# Revit family: JOMA_Spikplåtsvinklar
name_source: partatom
category: Structural Connections
revit_build: Autodesk Revit Structure 2012 (Build: 20110309_2315(x64)
units: mm (PartAtom-declared; Revit-internal decimal feet)

## types (22) — shared parameters
Länk Joma Dimensioneringsverktyg = http://www.joma.se
Material = Varmförzinkad stålplåt
zero-valued in all types: Default Elevation

## per-type parameters (varying)
| type | Spikplåtsvinkel 5511060 | Spikplåtsvinkel 5511080 | Spikplåtsvinkel 5511100 | Spikplåtsvinkel 5512100 | Spikplåtsvinkel 5546060 & 5524660 | Spikplåtsvinkel 5566060 & 5526660 | Spikplåtsvinkel 5566080 & 5526680 | Spikplåtsvinkel 5566100 & 55266100 | Spikplåtsvinkel 5568060 & 5526860 | Spikplåtsvinkel 5588040 & 5528840 | Spikplåtsvinkel 5588060 & 5528860 | Spikplåtsvinkel 5588080 & 5528880 | Spikplåtsvinkel 5588100 | Spikplåtsvinkel 5588120 | Typ | Vikt | b | h | ir | l | t | yr |
| 5526660  2,0x60x60x60 | No | No | No | No | No | Yes | No | No | No | No | No | No | No | No | SPIKPLÅTSVINKEL 5526660 | 0,11 | 60 mm  [stored 0.19685 ft] | 62 mm | 2.562 mm | 62 mm | 2 mm  [stored 0.00656168 ft] | 4.562 mm |
| 5526680  2,0x60x60x80 | No | No | No | No | No | No | Yes | No | No | No | No | No | No | No | SPIKPLÅTSVINKEL 5526680 | 0,15 | 80 mm | 62 mm | 2.562 mm | 62 mm | 2 mm  [stored 0.00656168 ft] | 4.562 mm |
| 55266100  2,0x60x60x100 | No | No | No | No | No | No | No | Yes | No | No | No | No | No | No | SPIKPLÅTSVINKEL 55266100 | 0,18 | 100 mm  [stored 0.328084 ft] | 62 mm | 2.562 mm | 62 mm | 2 mm  [stored 0.00656168 ft] | 4.562 mm |
| 5528840  2,0x80x80x40 | No | No | No | No | No | No | No | No | No | Yes | No | No | No | No | SPIKPLÅTSVINKEL 5528840 | 0,10 | 40 mm | 82 mm | 2.562 mm | 82 mm | 2 mm  [stored 0.00656168 ft] | 4.562 mm |
| 5528860  2,0x80x80x60 | No | No | No | No | No | No | No | No | No | No | Yes | No | No | No | SPIKPLÅTSVINKEL 5528860 | 0,15 | 60 mm  [stored 0.19685 ft] | 82 mm | 2.562 mm | 82 mm | 2 mm  [stored 0.00656168 ft] | 4.562 mm |
| 5528880  2,0x80x80x80 | No | No | No | No | No | No | No | No | No | No | No | Yes | No | No | SPIKPLÅTSVINKEL 5528880 | 0,19 | 80 mm | 82 mm | 2.562 mm | 82 mm | 2 mm  [stored 0.00656168 ft] | 4.562 mm |
| 5546060  2,5x40x60x60 | No | No | No | No | Yes | No | No | No | No | No | No | No | No | No | SPIKPLÅTSVINKEL 5546060 | 0,11 | 60 mm  [stored 0.19685 ft] | 62.5 mm | 3.203 mm | 42.5 mm | 2.5 mm  [stored 0.0082021 ft] | 5.703 mm |
| 5566060  2,5x60x60x60 | No | No | No | No | No | Yes | No | No | No | No | No | No | No | No | SPIKPLÅTSVINKEL 5566060 | 0,13 | 60 mm  [stored 0.19685 ft] | 62.5 mm | 3.202 mm | 62.5 mm | 2.5 mm  [stored 0.0082021 ft] | 5.702 mm |
| 5566080  2,5x60x60x80 | No | No | No | No | No | No | Yes | No | No | No | No | No | No | No | SPIKPLÅTSVINKEL 5566080 | 0,18 | 80 mm | 62.5 mm | 3.202 mm | 62.5 mm | 2.5 mm  [stored 0.0082021 ft] | 5.702 mm |
| 5566100  2,5x60x60x100 | No | No | No | No | No | No | No | Yes | No | No | No | No | No | No | SPIKPLÅTSVINKEL 5566100 | 0,22 | 100 mm  [stored 0.328084 ft] | 62.5 mm | 3.202 mm | 62.5 mm | 2.5 mm  [stored 0.0082021 ft] | 5.702 mm |
| 5568060  2,5x60x80x60 | No | No | No | No | No | No | No | No | Yes | No | No | No | No | No | SPIKPLÅTSVINKEL 5568060 | 0,15 | 60 mm  [stored 0.19685 ft] | 82.5 mm | 3.203 mm | 62.5 mm | 2.5 mm  [stored 0.0082021 ft] | 5.703 mm |
| 5588040  2,5x80x80x40 | No | No | No | No | No | No | No | No | No | Yes | No | No | No | No | SPIKPLÅTSVINKEL 5588040 | 0,12 | 40 mm | 82.5 mm | 3.202 mm | 82.5 mm | 2.5 mm  [stored 0.0082021 ft] | 5.702 mm |
| 5588060  2,5x80x80x60 | No | No | No | No | No | No | No | No | No | No | Yes | No | No | No | SPIKPLÅTSVINKEL 5588060 | 0,17 | 60 mm  [stored 0.19685 ft] | 82.5 mm | 3.203 mm | 82.5 mm | 2.5 mm  [stored 0.0082021 ft] | 5.703 mm |
| 5588080  2,5x80x80x80 | No | No | No | No | No | No | No | No | No | No | No | Yes | No | No | SPIKPLÅTSVINKEL 5588080 | 0,23 | 80 mm | 82.5 mm | 3.203 mm | 82.5 mm | 2.5 mm  [stored 0.0082021 ft] | 5.703 mm |
| 5588100  2,5x80x80x100 | No | No | No | No | No | No | No | No | No | No | No | No | Yes | No | SPIKPLÅTSVINKEL 5588100 | 0,31 | 100 mm  [stored 0.328084 ft] | 82.5 mm | 3.203 mm | 82.5 mm | 2.5 mm  [stored 0.0082021 ft] | 5.703 mm |
| 5588120  2,5x80x80x120 | No | No | No | No | No | No | No | No | No | No | No | No | No | Yes | SPIKPLÅTSVINKEL 5588120 | 0,34 | 120 mm | 82.5 mm | 3.202 mm | 82.5 mm | 2.5 mm  [stored 0.0082021 ft] | 5.702 mm |
| 5511060  2,5x100x100x60 | Yes | No | No | No | No | No | No | No | No | No | No | No | No | No | SPIKPLÅTSVINKEL 5511060 | 0,21 | 60 mm  [stored 0.19685 ft] | 102.5 mm | 3.203 mm | 102.5 mm | 2.5 mm  [stored 0.0082021 ft] | 5.703 mm |
| 5511080  2,5x100x100x80 | No | Yes | No | No | No | No | No | No | No | No | No | No | No | No | SPIKPLÅTSVINKEL 5511080 | 0,29 | 80 mm | 102.5 mm | 3.203 mm | 102.5 mm | 2.5 mm  [stored 0.0082021 ft] | 5.703 mm |
| 5511100  2,5x100x100x100 | No | No | Yes | No | No | No | No | No | No | No | No | No | No | No | SPIKPLÅTSVINKEL 5511100 | 0,36 | 100 mm  [stored 0.328084 ft] | 102.5 mm | 3.203 mm | 102.5 mm | 2.5 mm  [stored 0.0082021 ft] | 5.703 mm |
| 5512100  2,5x100x200x100 | No | No | No | Yes | No | No | No | No | No | No | No | No | No | No | SPIKPLÅTSVINKEL 5512100 | 0,21 | 100 mm  [stored 0.328084 ft] | 202.5 mm | 3.202 mm | 102.5 mm | 2.5 mm  [stored 0.0082021 ft] | 5.702 mm |
| 5524660  2,0x40x60x60 | No | No | No | No | Yes | No | No | No | No | No | No | No | No | No | SPIKPLÅTSVINKEL 5524660 | 0,11 | 60 mm  [stored 0.19685 ft] | 62 mm | 2.562 mm | 42 mm | 2 mm  [stored 0.00656168 ft] | 4.562 mm |
| 5526860  2,0x60x80x60 | No | No | No | No | No | No | No | No | Yes | No | No | No | No | No | SPIKPLÅTSVINKEL 5526860 | 0,15 | 60 mm  [stored 0.19685 ft] | 82 mm | 2.562 mm | 62 mm | 2 mm  [stored 0.00656168 ft] | 4.562 mm |

note: [stored X ft] marks values corroborated as IEEE doubles in the binary element streams (Revit-internal decimal feet)

## geometry (parser evidence)
native form markers: Sweep x4
no freeform markers — native parametric forms only
